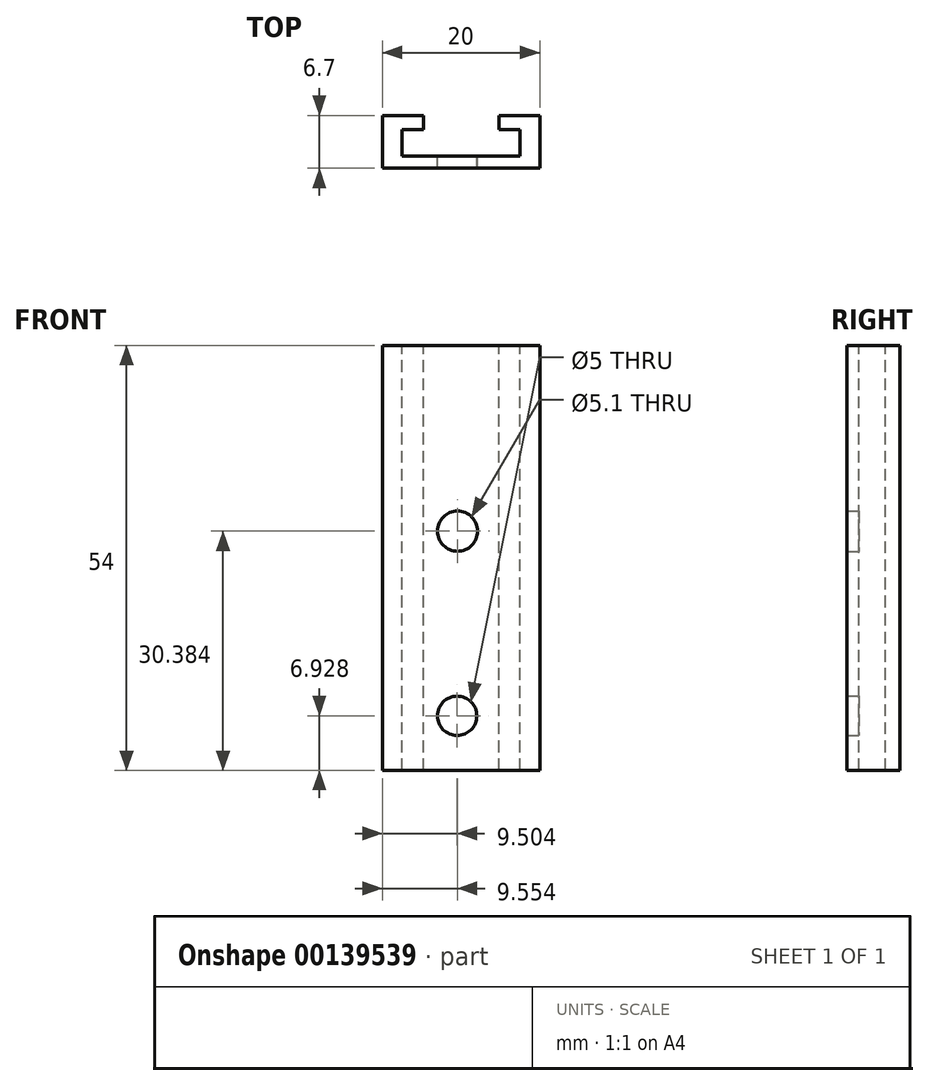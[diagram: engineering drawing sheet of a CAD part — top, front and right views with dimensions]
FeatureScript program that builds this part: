
annotation { "Feature Type Name" : "Feature", "Feature Type Description" : "" }
export const myFeature = defineFeature(function(context is Context, id is Id, definition is map)
    precondition{}
    {
        {
            var Q0;
            Q0=qCreatedBy(makeId("Front.planeOp"),FACE);
            var sketch = newSketch(context, id + "F0", { "sketchPlane" : qUnion([Q0])});
            skLineSegment(sketch, "E0.bottom", {"start": v(-35.6, 43.16) * mm, "end": v(-15.6, 43.16) * mm});
            skLineSegment(sketch, "E0.top", {"start": v(-35.6, -10.84) * mm, "end": v(-15.6, -10.84) * mm});
            skLineSegment(sketch, "E0.left", {"start": v(-35.6, 43.16) * mm, "end": v(-35.6, -10.84) * mm});
            skLineSegment(sketch, "E0.right", {"start": v(-15.6, 43.16) * mm, "end": v(-15.6, -10.84) * mm});
            skSolve(sketch);
        }
        {
            var Q0;
            Q0=makeQuery(id+"F0.imprint","IMPRINT",FACE,{"disambiguationData":[TD([[makeQuery(id+"F0.imprint","IMPRINT",EDGE,{"derivedFrom":sQuery(id+"F0.wireOp",EDGE,"E0.bottom")}),-1.0]])]});
            extrude(context, id + "F1", {"entities" : qUnion([Q0]), "depth" : 6.7 * mm});
        }
        {
            var Q0;
            Q0=makeQuery(id+"F1.opExtrude","SWEPT_FACE",FACE,{"disambiguationData":[OSD([sQuery(id+"F0.wireOp",EDGE,"E0.bottom")])]});
            var sketch = newSketch(context, id + "F2", { "sketchPlane" : qUnion([Q0])});
            skLineSegment(sketch, "E1", {"start": v(-20.8, 0) * mm, "end": v(-20.8, -1.81) * mm});
            skLineSegment(sketch, "E2", {"start": v(-20.8, -1.81) * mm, "end": v(-18.1, -1.81) * mm});
            skLineSegment(sketch, "E3", {"start": v(-18.1, -1.81) * mm, "end": v(-18.1, -5.2) * mm});
            skLineSegment(sketch, "E4", {"start": v(-18.1, -5.2) * mm, "end": v(-33.1, -5.2) * mm});
            skLineSegment(sketch, "E5", {"start": v(-33.1, -5.2) * mm, "end": v(-33.1, -1.81) * mm});
            skLineSegment(sketch, "E6", {"start": v(-33.1, -1.81) * mm, "end": v(-30.4, -1.81) * mm});
            skLineSegment(sketch, "E7", {"start": v(-30.4, -1.81) * mm, "end": v(-30.4, 0) * mm});
            skLineSegment(sketch, "E8", {"start": v(-30.4, 0) * mm, "end": v(-20.8, 0) * mm});
            skSolve(sketch);
        }
        {
            var Q0;
            Q0 = qSketchRegion(id + "F2", true);
            extrude(context, id + "F3", {"entities" : qUnion([Q0]), "operationType" : NewBodyOperationType.REMOVE, "oppositeDirection" : true, "depth" : 67.5 * mm});
        }
        {
            var Q0;
            Q0=makeQuery(id+"F3.boolean.opBoolean","COPY",FACE,{"derivedFrom":makeQuery(id+"F3.opExtrude","SWEPT_FACE",FACE,{"disambiguationData":[OSD([sQuery(id+"F2.wireOp",EDGE,"E4")])]})});
            var sketch = newSketch(context, id + "F4", { "sketchPlane" : qUnion([Q0])});
            skCircle(sketch, "E9", {"center": v(26.1, -3.91) * mm, "radius": 2.5 * mm});
            skCircle(sketch, "E10", {"center": v(26.05, 19.54) * mm, "radius": 2.55 * mm});
            skSolve(sketch);
        }
        {
            var Q0;
            Q0=makeQuery(id+"F4.imprint","IMPRINT",FACE,{"disambiguationData":[TD([[makeQuery(id+"F4.imprint","IMPRINT",EDGE,{"derivedFrom":sQuery(id+"F4.wireOp",EDGE,"E10")}),1.0]])]});
            var Q1;
            Q1=makeQuery(id+"F4.imprint","IMPRINT",FACE,{"disambiguationData":[TD([[makeQuery(id+"F4.imprint","IMPRINT",EDGE,{"derivedFrom":sQuery(id+"F4.wireOp",EDGE,"E9")}),1.0]])]});
            var Q2;
            Q2=sQuery(id+"F4.wireOp",EDGE,"E10");
            var Q3;
            Q3=sQuery(id+"F4.wireOp",EDGE,"E9");
            extrude(context, id + "F5", {"entities" : qUnion([Q0, Q1]), "operationType" : NewBodyOperationType.REMOVE, "surfaceEntities" : qUnion([Q2, Q3]), "oppositeDirection" : true, "depth" : 25 * mm});
        }
    });
